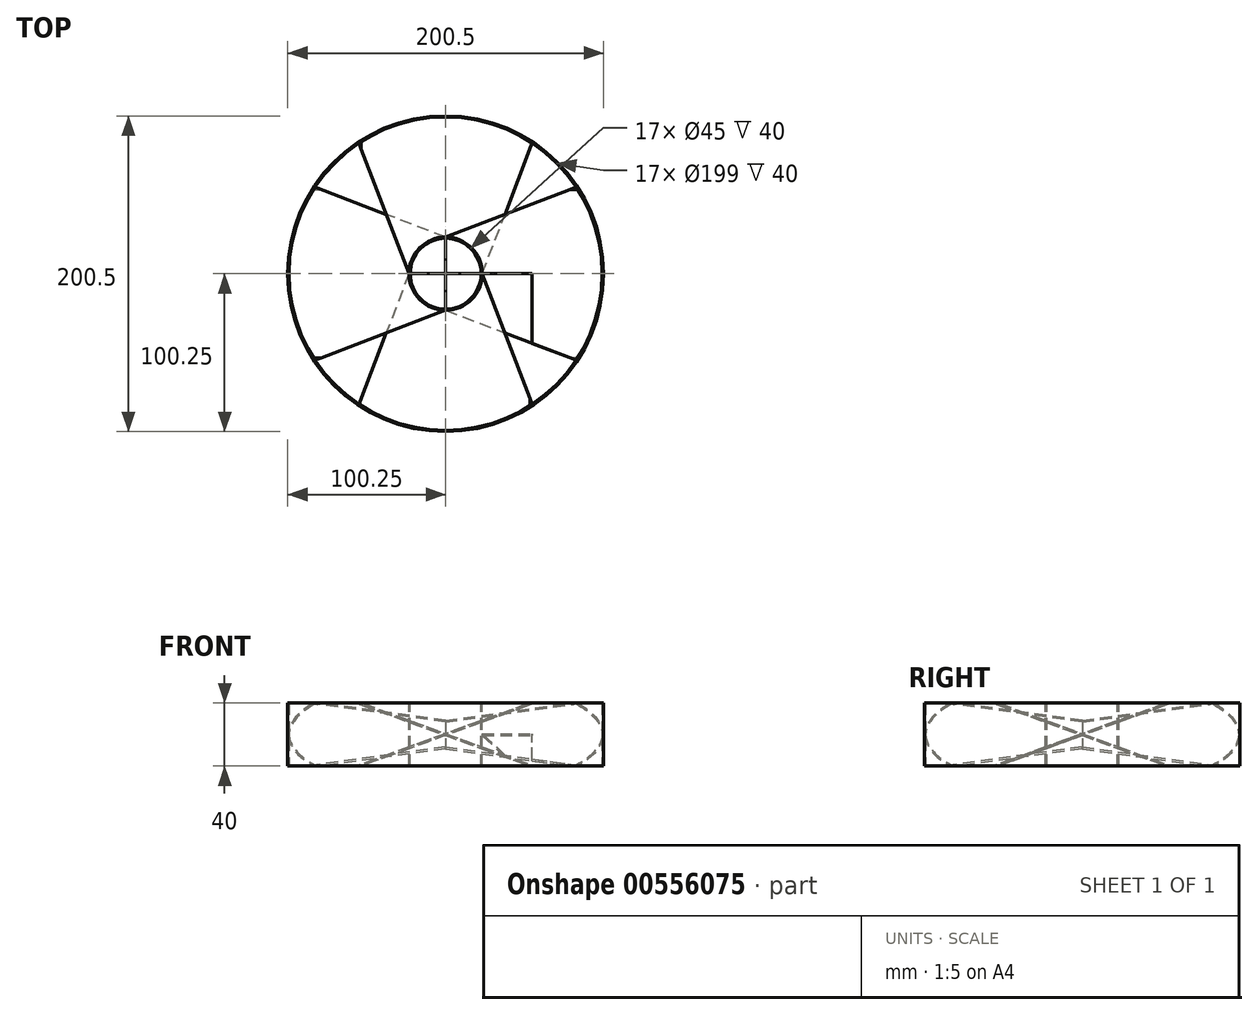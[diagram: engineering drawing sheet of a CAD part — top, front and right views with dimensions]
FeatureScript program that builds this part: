
annotation { "Feature Type Name" : "Feature", "Feature Type Description" : "" }
export const myFeature = defineFeature(function(context is Context, id is Id, definition is map)
    precondition{}
    {
        {
            var Q0;
            Q0=qCreatedBy(makeId("Top.planeOp"),FACE);
            var sketch = newSketch(context, id + "F0", { "sketchPlane" : qUnion([Q0])});
            skCircle(sketch, "E0", {"center": v(0, 0) * mm, "radius": 23.25 * mm});
            skCircle(sketch, "E1", {"center": v(0, 0) * mm, "radius": 22.5 * mm});
            skSolve(sketch);
        }
        {
            var Q0;
            Q0=makeQuery(id+"F0.imprint","IMPRINT",FACE,{"disambiguationData":[TD([[makeQuery(id+"F0.imprint","IMPRINT",EDGE,{"derivedFrom":sQuery(id+"F0.wireOp",EDGE,"E0")}),1.0]])]});
            extrude(context, id + "F1", {"entities" : qUnion([Q0]), "depth" : 140 * mm, "offsetDistance" : 25 * mm});
        }
        {
            var Q0;
            Q0=qCreatedBy(makeId("Top.planeOp"),FACE);
            cPlane(context, id + "F2", {"entities" : qUnion([Q0]), "cplaneType" : CPlaneType.OFFSET, "offset" : 140 * mm, "width" : 150 * mm, "height" : 150 * mm});
        }
        {
            var Q0;
            Q0=qCreatedBy(id+"F2.planeOp",FACE);
            var sketch = newSketch(context, id + "F3", { "sketchPlane" : qUnion([Q0])});
            skCircle(sketch, "E2", {"center": v(0, 0) * mm, "radius": 99.5 * mm});
            skCircle(sketch, "E3", {"center": v(0, 0) * mm, "radius": 100.25 * mm});
            skSolve(sketch);
        }
        {
            var Q0;
            Q0=makeQuery(id+"F3.imprint","IMPRINT",FACE,{"disambiguationData":[TD([[makeQuery(id+"F3.imprint","IMPRINT",EDGE,{"derivedFrom":sQuery(id+"F3.wireOp",EDGE,"E2")}),-1.0]])]});
            extrude(context, id + "F4", {"entities" : qUnion([Q0]), "oppositeDirection" : true, "depth" : 40 * mm, "offsetDistance" : 25 * mm});
        }
        {
            var Q0;
            Q0=qCreatedBy(makeId("Front.planeOp"),FACE);
            var sketch = newSketch(context, id + "F5", { "sketchPlane" : qUnion([Q0])});
            skLineSegment(sketch, "E4.0", {"start": v(-100.25, 140) * mm, "end": v(100.25, 140) * mm});
            skLineSegment(sketch, "E5.0", {"start": v(-100.25, 100) * mm, "end": v(100.25, 100) * mm});
            skLineSegment(sketch, "E6", {"start": v(0, 100) * mm, "end": v(0, 140) * mm, "construction": true});
            skLineSegment(sketch, "E7.bottom", {"start": v(55, 140) * mm, "end": v(-55, 140) * mm});
            skLineSegment(sketch, "E7.top", {"start": v(55, 100) * mm, "end": v(-55, 100) * mm});
            skLineSegment(sketch, "E7.left", {"start": v(55, 140.17) * mm, "end": v(55, 140) * mm});
            skLineSegment(sketch, "E7.right", {"start": v(-55, 100) * mm, "end": v(-55, 99.83) * mm});
            skPoint(sketch, "E7.middle", {"position": v(0, 120) * mm});
            skLineSegment(sketch, "E8.0", {"start": v(-54.34, 100.77) * mm, "end": v(53.54, 140) * mm});
            skLineSegment(sketch, "E9.0", {"start": v(-53.54, 100) * mm, "end": v(54.34, 139.23) * mm});
            skArc(sketch, "E10.filletArc", {"start": v(54.34, 139.23) * mm, "mid": v(54.82, 139.6) * mm, "end": v(55, 140.17) * mm});
            skArc(sketch, "E11.filletArc", {"start": v(-54.34, 100.77) * mm, "mid": v(-54.82, 100.4) * mm, "end": v(-55, 99.83) * mm});
            skSolve(sketch);
        }
        {
            var Q0;
            {var subQ4=sQuery(id+"F5.wireOp",EDGE,"E8.0");Q0=makeQuery(id+"F5.imprint","IMPRINT",FACE,{"disambiguationData":[TD([[makeQuery(id+"F5.imprint","IMPRINT",EDGE,{"derivedFrom":subQ4}),-1.0]])]});}
            var Q1;
            Q1=makeQuery(id+"F4.opExtrude","SWEPT_FACE",FACE,{"disambiguationData":[OSD([sQuery(id+"F3.wireOp",EDGE,"E2")])]});
            extrude(context, id + "F6", {"entities" : qUnion([Q0]), "endBound" : BoundingType.UP_TO_SURFACE, "depth" : 25 * mm, "endBoundEntityFace" : qUnion([Q1]), "offsetDistance" : 25 * mm});
        }
        {
            var Q0;
            Q0=qCreatedBy(id+"F2.planeOp",FACE);
            var sketch = newSketch(context, id + "F7", { "sketchPlane" : qUnion([Q0])});
            skCircle(sketch, "E12.0", {"center": v(0, 0) * mm, "radius": 23.25 * mm});
            skLineSegment(sketch, "E13.0", {"start": v(-54.34, 0) * mm, "end": v(53.54, 0) * mm});
            skCircle(sketch, "E14.0", {"center": v(0, 0) * mm, "radius": 99.5 * mm});
            skLineSegment(sketch, "E15.0", {"start": v(-54.99, -82.93) * mm, "end": v(-54.99, 0) * mm});
            skLineSegment(sketch, "E16.0", {"start": v(54.99, -82.93) * mm, "end": v(54.99, 0) * mm});
            skLineSegment(sketch, "E17", {"start": v(-23.25, 0) * mm, "end": v(-54.99, -82.93) * mm});
            skLineSegment(sketch, "E18", {"start": v(-23.25, 0) * mm, "end": v(-54.99, 0) * mm});
            skSolve(sketch);
        }
        {
            var Q0;
            {var subQ0=sQuery(id+"F7.wireOp",EDGE,"E17");Q0=makeQuery(id+"F7.imprint","IMPRINT",FACE,{"disambiguationData":[TD([[makeQuery(id+"F7.imprint","IMPRINT",EDGE,{"derivedFrom":subQ0}),-1.0]])]});}
            extrude(context, id + "F8", {"entities" : qUnion([Q0]), "operationType" : NewBodyOperationType.REMOVE, "oppositeDirection" : true, "depth" : 50 * mm, "offsetDistance" : 25 * mm});
        }
        {
            var Q0;
            Q0=qCreatedBy(makeId("Top.planeOp"),FACE);
            var sketch = newSketch(context, id + "F9", { "sketchPlane" : qUnion([Q0])});
            skLineSegment(sketch, "E19.0", {"start": v(-23.25, 0) * mm, "end": v(53.54, 0) * mm});
            skCircle(sketch, "E20.0", {"center": v(0, 0) * mm, "radius": 23.25 * mm});
            skLineSegment(sketch, "E21.0", {"start": v(54.99, -82.93) * mm, "end": v(54.99, 0) * mm});
            skCircle(sketch, "E22.0", {"center": v(0, 0) * mm, "radius": 99.5 * mm});
            skLineSegment(sketch, "E23", {"start": v(23.25, 0) * mm, "end": v(54.99, 0) * mm});
            skLineSegment(sketch, "E24", {"start": v(54.99, -82.93) * mm, "end": v(23.25, 0) * mm});
            skSolve(sketch);
        }
        {
            var Q0;
            {var subQ0=sQuery(id+"F9.wireOp",EDGE,"E21.0");Q0=makeQuery(id+"F9.imprint","IMPRINT",FACE,{"disambiguationData":[TD([[makeQuery(id+"F9.imprint","IMPRINT",EDGE,{"derivedFrom":subQ0}),1.0]])]});}
            extrude(context, id + "F10", {"entities" : qUnion([Q0]), "operationType" : NewBodyOperationType.REMOVE, "depth" : 150 * mm, "offsetDistance" : 25 * mm});
        }
        {
            var Q0;
            Q0=makeQuery(id+"F6.opExtrude","SWEPT_BODY",BODY,{"disambiguationData":[OSD([sQuery(id+"F5.wireOp",EDGE,"E7.bottom"),sQuery(id+"F5.wireOp",EDGE,"E7.top"),sQuery(id+"F5.wireOp",EDGE,"E8.0"),sQuery(id+"F5.wireOp",EDGE,"E9.0"),sQuery(id+"F5.wireOp",EDGE,"E10.filletArc"),sQuery(id+"F5.wireOp",EDGE,"E11.filletArc")])]});
            var Q1;
            Q1=makeQuery(id+"F1.opExtrude","SWEPT_FACE",FACE,{"disambiguationData":[OSD([sQuery(id+"F0.wireOp",EDGE,"E0")])]});
            circularPattern(context, id + "F11", {"entities" : qUnion([Q0]), "axis" : qUnion([Q1]), "angle" : 360 * degree, "instanceCount" : 4, "equalSpace" : true});
        }
        {
            var Q0;
            Q0=qCreatedBy(makeId("Top.planeOp"),FACE);
            cPlane(context, id + "F12", {"entities" : qUnion([Q0]), "cplaneType" : CPlaneType.OFFSET, "offset" : 70 * mm, "width" : 150 * mm, "height" : 150 * mm});
        }
        {
            var Q0;
            Q0=qCreatedBy(id+"F12.planeOp",FACE);
            var sketch = newSketch(context, id + "F13", { "sketchPlane" : qUnion([Q0])});
            skLineSegment(sketch, "E25", {"start": v(0, 0) * mm, "end": v(53.23, 0) * mm, "construction": true});
            skSolve(sketch);
        }
        {
            var Q0;
            Q0=makeQuery(id+"F11.opPattern","COPY",BODY,{"derivedFrom":makeQuery(id+"F6.opExtrude","SWEPT_BODY",BODY,{"disambiguationData":[OSD([sQuery(id+"F5.wireOp",EDGE,"E7.bottom"),sQuery(id+"F5.wireOp",EDGE,"E7.top"),sQuery(id+"F5.wireOp",EDGE,"E8.0"),sQuery(id+"F5.wireOp",EDGE,"E9.0"),sQuery(id+"F5.wireOp",EDGE,"E10.filletArc"),sQuery(id+"F5.wireOp",EDGE,"E11.filletArc")])]}),"instanceName":"3"});
            var Q1;
            Q1=makeQuery(id+"F1.opExtrude","SWEPT_BODY",BODY,{"disambiguationData":[OSD([sQuery(id+"F0.wireOp",EDGE,"E0"),sQuery(id+"F0.wireOp",EDGE,"E1")])]});
            var Q2;
            Q2=makeQuery(id+"F6.opExtrude","SWEPT_BODY",BODY,{"disambiguationData":[OSD([sQuery(id+"F5.wireOp",EDGE,"E7.bottom"),sQuery(id+"F5.wireOp",EDGE,"E7.top"),sQuery(id+"F5.wireOp",EDGE,"E8.0"),sQuery(id+"F5.wireOp",EDGE,"E9.0"),sQuery(id+"F5.wireOp",EDGE,"E10.filletArc"),sQuery(id+"F5.wireOp",EDGE,"E11.filletArc")])]});
            var Q3;
            Q3=makeQuery(id+"F11.opPattern","COPY",BODY,{"derivedFrom":makeQuery(id+"F6.opExtrude","SWEPT_BODY",BODY,{"disambiguationData":[OSD([sQuery(id+"F5.wireOp",EDGE,"E7.bottom"),sQuery(id+"F5.wireOp",EDGE,"E7.top"),sQuery(id+"F5.wireOp",EDGE,"E8.0"),sQuery(id+"F5.wireOp",EDGE,"E9.0"),sQuery(id+"F5.wireOp",EDGE,"E10.filletArc"),sQuery(id+"F5.wireOp",EDGE,"E11.filletArc")])]}),"instanceName":"1"});
            var Q4;
            Q4=makeQuery(id+"F4.opExtrude","SWEPT_BODY",BODY,{"disambiguationData":[OSD([sQuery(id+"F3.wireOp",EDGE,"E2"),sQuery(id+"F3.wireOp",EDGE,"E3")])]});
            var Q5;
            Q5=makeQuery(id+"F11.opPattern","COPY",BODY,{"derivedFrom":makeQuery(id+"F6.opExtrude","SWEPT_BODY",BODY,{"disambiguationData":[OSD([sQuery(id+"F5.wireOp",EDGE,"E7.bottom"),sQuery(id+"F5.wireOp",EDGE,"E7.top"),sQuery(id+"F5.wireOp",EDGE,"E8.0"),sQuery(id+"F5.wireOp",EDGE,"E9.0"),sQuery(id+"F5.wireOp",EDGE,"E10.filletArc"),sQuery(id+"F5.wireOp",EDGE,"E11.filletArc")])]}),"instanceName":"2"});
            var Q6;
            Q6=sQuery(id+"F13.wireOp",EDGE,"E25");
            var Q7;
            Q7=sQuery(id+"F13.wireOp",EDGE,"E25");
            transform(context, id + "F14", {"entities" : qUnion([Q0, Q1, Q2, Q3, Q4, Q5]), "transformType" : TransformType.ROTATION, "transformAxis" : qUnion([Q7]), "angle" : 180 * degree, "makeCopy" : false});
        }
        {
            var Q0;
            Q0=qCreatedBy(id+"F2.planeOp",FACE);
            var sketch = newSketch(context, id + "F15", { "sketchPlane" : qUnion([Q0])});
            skCircle(sketch, "E26", {"center": v(0, 0) * mm, "radius": 43.23 * mm});
            skSolve(sketch);
        }
        {
            var Q0;
            Q0=makeQuery(id+"F15.imprint","IMPRINT",FACE,{"disambiguationData":[TD([[makeQuery(id+"F15.imprint","IMPRINT",EDGE,{"derivedFrom":sQuery(id+"F15.wireOp",EDGE,"E26")}),1.0]])]});
            extrude(context, id + "F16", {"entities" : qUnion([Q0]), "operationType" : NewBodyOperationType.REMOVE, "oppositeDirection" : true, "depth" : 100 * mm, "offsetDistance" : 25 * mm});
        }
    });
